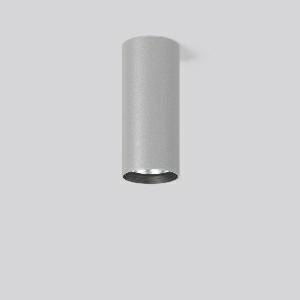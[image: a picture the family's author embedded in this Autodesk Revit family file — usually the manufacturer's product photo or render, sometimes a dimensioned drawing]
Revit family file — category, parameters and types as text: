
# Revit family: heledon_mini_a_931208_004_3_8543
name_source: partatom
category: Lighting Fixtures
units: mm (PartAtom-declared; Revit-internal decimal feet)

## family parameters
Cut with Voids When Loaded = No
Host = Face
Light Source = No
Part Type = Normal
Room Calculation Point = No
Round Connector Dimension = Use Diameter
Shared = No

## types (1)
- HELEDON mini A (1 x LED Modul 935, 3700 lm, 3500)
    Apparent Load = 29 VA
    Approval mark = CE
    CIE Flux Codes = 100 100 100 100 100
    Color Rendering = 92
    Color Temperature = 3500
    Default Elevation = 1800 mm
    Description = Series: HELEDON mini
Cylindrical surface-mounted downlight. Housing: die-cast aluminium, powder-coated. Internal ceiling frame polycarbonate with bayonet mounting. Black plastic ring and recessed LED to prevent glare from the side. Optical assembly with reflector made of MIRO-Silver with 98% total light reflection for outstanding efficiency - can be changed without tools. Best colour rendering index Ra>90. Suitable for Ceiling mounting. Easy installation with a separate ceiling frame with bayonet mounting and plug connection. Driver integrated. Connected via plug-in connector. High quality converter without flickering and stroboscopic effect. The following accessories can be mounted without use of tools: interchangeable lenses, decorative glasses, honeycomb louvre, clear and frosted diffusers, white interchangeable plastic ring. 
Colour: silver
Diameter: 87 mm
Height: 197 mm
Lamp: LED
Socket: without socket
Colour temperature: 3500K
Colour rendering index (CRI): 92
System power: 29 W
Rated luminous flux: 3700 lm
Luminous efficiency: 128 lm/W
Control gear: Regulated power supply
Protection class: I
Type of protection: IP 20
    Height = 197 mm
    Lamp = 1 x LED Modul 935
    Lamp Light Flux = 3700 lm
    Lamp count = 1
    Length = 87 mm
    Lifetime = 50000 h
    Luminous efficacy = 128 lm/W
    Manufacturer = RZB
    ModVariant = No
    Model = 931208.004.3
    Mounting Place = Ceiling
    Mounting Type = Surface mounted
    Number of Poles = 1
    OnlyDefault = Yes
    Power Factor = 1
    Product Name = HELEDON mini A
    Product group = Surface mounted downlights
    ProductGroupID = 302
    Protection Class = Protection class I
    Protection Degree = IP 20
    RLX_Detail_Level = 1
    RLX_Emergency_Light_Flux = 0 lm
    RLX_Emergency_Type = 0
    RLX_Emergency_Type_DB = No
    RlxData = <blob elided: 109049 chars, md5=b1ce2aed>
    Socket = socket
    Standby Power = 0 W
    System Light Flux = 3700 lm
    System Power = 29 W
    Type Comments = Product without accessories
    Type Image = 931188.004.jpg
    URL = http://relux.com
    VarID = ---
    Voltage = 230 V
    Voltage Range = 220-240 V
    Weight = 0.00 kg
    Width = 0 mm  [stored 0 ft]

note: [stored X ft] marks values corroborated as IEEE doubles in the binary element streams (Revit-internal decimal feet)

## geometry (parser evidence)
native form markers: Blend x4, Sweep x9
no freeform markers — native parametric forms only
